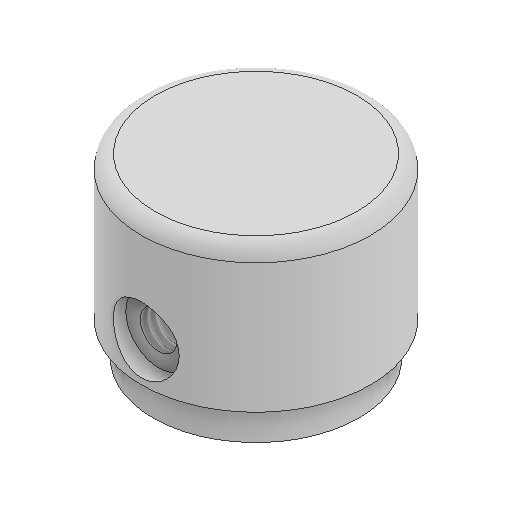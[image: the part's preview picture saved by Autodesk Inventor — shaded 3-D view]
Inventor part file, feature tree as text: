
AUTODESK INVENTOR PART (.ipt)
format: ipt  version: 2025 (Build 290162000, 162)  size: 158,720 bytes
history: native  units: mm
features: sketch x2, revolve x1, fillet x1, plane x1, hole x1
ambient origin geometry x8: Origin, YZ Plane, XZ Plane, XY Plane, X Axis, Y Axis, Z Axis, Center Point
bodies: Solid1 (feature_tree)
feature tree (6):
  revolve  "Revolution1"  [1 undecoded]
  fillet  "Fillet1"  Radius=3.0mm
  plane  "Work Plane1"
  hole  "Hole1"  [1 undecoded]
  sketch  "Sketch1"  dims[d0=15.5mm d1=12.0mm d2=3.0mm]
  sketch  "Sketch3"  dims[d4=6.0mm d5=15.0mm d6=18.0mm d7=20.0mm d8=90.0deg d9=1.2mm d11=6.4mm d12=3.242mm d13=8.0mm d14=5.75mm d15=1.5mm d16=90.0deg d17=8.0mm d18=20.594885mm]
note: 2 required parameter values undecoded (feature->parameter linkage not recoverable at this tier; creation-order binding heuristic only, values carry confidence <= 0.55)